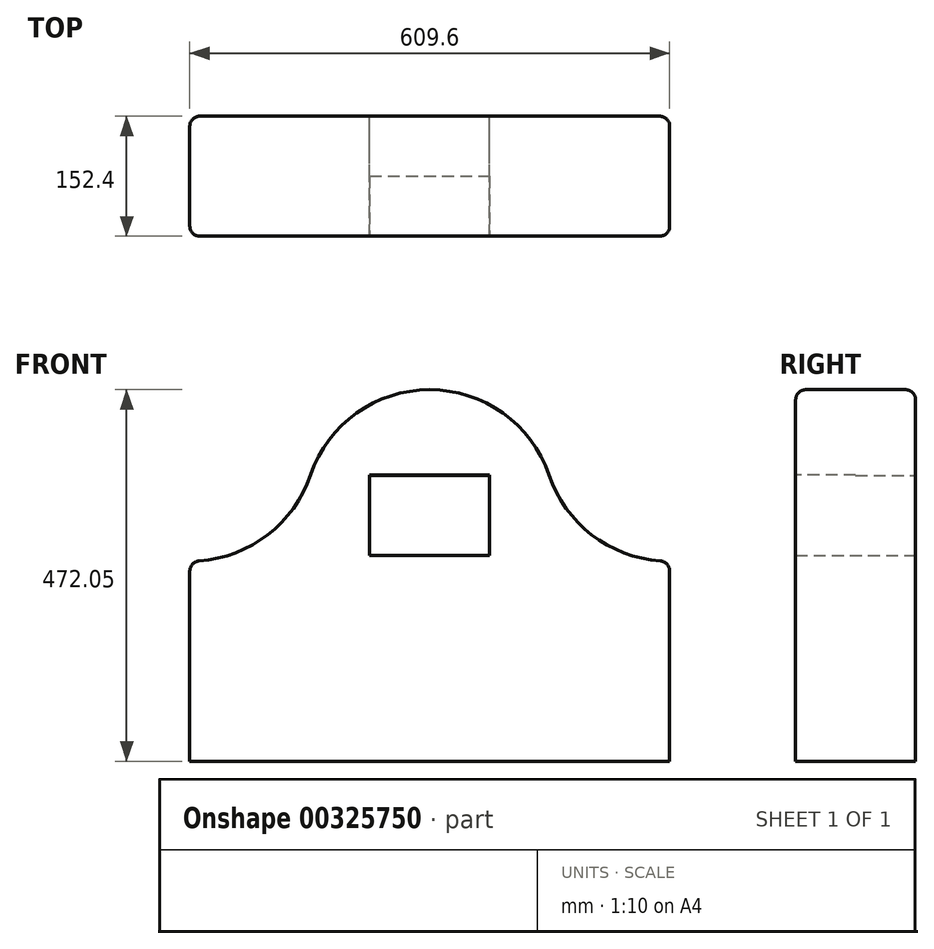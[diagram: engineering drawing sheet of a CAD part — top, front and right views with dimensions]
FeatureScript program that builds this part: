
annotation { "Feature Type Name" : "Feature", "Feature Type Description" : "" }
export const myFeature = defineFeature(function(context is Context, id is Id, definition is map)
    precondition{}
    {
        {
            var Q0;
            Q0=qCreatedBy(makeId("Front.planeOp"),FACE);
            var sketch = newSketch(context, id + "F0", { "sketchPlane" : qUnion([Q0])});
            skLineSegment(sketch, "E0.top", {"start": v(0, -254) * mm, "end": v(609.6, -254) * mm});
            skLineSegment(sketch, "E0.left", {"start": v(0, 0) * mm, "end": v(0, -254) * mm});
            skLineSegment(sketch, "E0.right", {"start": v(609.6, 0) * mm, "end": v(609.6, -254) * mm});
            skArc(sketch, "E1", {"start": v(0, 0) * mm, "mid": v(94.32, 30.26) * mm, "end": v(153.43, 109.76) * mm});
            skArc(sketch, "E2.MirrorCS", {"start": v(609.6, 0) * mm, "mid": v(515.28, 30.26) * mm, "end": v(456.17, 109.76) * mm});
            skArc(sketch, "E3", {"start": v(456.17, 109.76) * mm, "mid": v(304.8, 218.05) * mm, "end": v(153.43, 109.76) * mm});
            skLineSegment(sketch, "E4.bottom", {"start": v(228.6, 108.9) * mm, "end": v(381, 108.9) * mm});
            skLineSegment(sketch, "E4.top", {"start": v(228.6, 7.3) * mm, "end": v(381, 7.3) * mm});
            skLineSegment(sketch, "E4.left", {"start": v(228.6, 108.9) * mm, "end": v(228.6, 7.3) * mm});
            skLineSegment(sketch, "E4.right", {"start": v(381, 108.9) * mm, "end": v(381, 7.3) * mm});
            skSolve(sketch);
        }
        {
            var Q0;
            {var subQ1=sQuery(id+"F0.wireOp",EDGE,"E1");Q0=makeQuery(id+"F0.imprint","IMPRINT",FACE,{"disambiguationData":[TD([[makeQuery(id+"F0.imprint","IMPRINT",EDGE,{"derivedFrom":subQ1}),-1.0]])]});}
            var Q1;
            {var subQ0=sQuery(id+"F0.wireOp",EDGE,"E0.left");Q1=makeQuery(id+"F0.imprint","IMPRINT",FACE,{"disambiguationData":[TD([[makeQuery(id+"F0.imprint","IMPRINT",EDGE,{"derivedFrom":subQ0}),1.0]])]});}
            var Q2;
            {var subQ0=sQuery(id+"F0.wireOp",EDGE,"E0.right");Q2=makeQuery(id+"F0.imprint","IMPRINT",FACE,{"disambiguationData":[TD([[makeQuery(id+"F0.imprint","IMPRINT",EDGE,{"derivedFrom":subQ0}),-1.0]])]});}
            extrude(context, id + "F1", {"entities" : qUnion([Q0, Q1, Q2]), "depth" : 152.4 * mm});
        }
        {
            var Q0;
            Q0=makeQuery(id+"F1.opExtrude","CAP_FACE",FACE,{"disambiguationData":[OSD([sQuery(id+"F0.wireOp",EDGE,"E0.top"),sQuery(id+"F0.wireOp",EDGE,"E0.left"),sQuery(id+"F0.wireOp",EDGE,"E0.right"),sQuery(id+"F0.wireOp",EDGE,"E1"),sQuery(id+"F0.wireOp",EDGE,"E2.MirrorCS"),sQuery(id+"F0.wireOp",EDGE,"E3")])],"isStart":false});
            var sketch = newSketch(context, id + "F2", { "sketchPlane" : qUnion([Q0])});
            skLineSegment(sketch, "E5.0.0", {"start": v(609.6, -254) * mm, "end": v(609.6, 0) * mm});
            skArc(sketch, "E5.0.1", {"start": v(609.6, 0) * mm, "mid": v(515.28, 30.26) * mm, "end": v(456.17, 109.76) * mm});
            skArc(sketch, "E5.0.2", {"start": v(456.17, 109.76) * mm, "mid": v(304.8, 218.05) * mm, "end": v(153.43, 109.76) * mm});
            skArc(sketch, "E5.0.3", {"start": v(153.43, 109.76) * mm, "mid": v(94.32, 30.26) * mm, "end": v(0, 0) * mm});
            skLineSegment(sketch, "E5.0.4", {"start": v(0, 0) * mm, "end": v(0, -254) * mm});
            skLineSegment(sketch, "E5.0.5", {"start": v(0, -254) * mm, "end": v(609.6, -254) * mm});
            skLineSegment(sketch, "E6.bottom", {"start": v(228.6, 109.76) * mm, "end": v(381, 109.76) * mm});
            skLineSegment(sketch, "E6.top", {"start": v(228.6, 0) * mm, "end": v(381, 0) * mm});
            skLineSegment(sketch, "E6.left", {"start": v(228.6, 109.76) * mm, "end": v(228.6, 0) * mm});
            skLineSegment(sketch, "E6.right", {"start": v(381, 109.76) * mm, "end": v(381, 0) * mm});
            skSolve(sketch);
        }
        {
            var Q0;
            Q0=makeQuery(id+"F2.imprint","IMPRINT",FACE,{"disambiguationData":[TD([[makeQuery(id+"F2.imprint","IMPRINT",EDGE,{"derivedFrom":sQuery(id+"F2.wireOp",EDGE,"E6.bottom")}),-1.0]])]});
            extrude(context, id + "F3", {"entities" : qUnion([Q0]), "operationType" : NewBodyOperationType.REMOVE, "oppositeDirection" : true, "depth" : 76.2 * mm});
        }
        {
            var Q0;
            Q0=makeQuery(id+"F1.opExtrude","SWEPT_EDGE",EDGE,{"disambiguationData":[OSD([sQuery(id+"F0.wireOp",EDGE,"E0.bottom"),sQuery(id+"F0.wireOp",EDGE,"E0.right"),sQuery(id+"F0.wireOp",EDGE,"E2.MirrorCS")])]});
            var Q1;
            Q1=makeQuery(id+"F1.opExtrude","SWEPT_EDGE",EDGE,{"disambiguationData":[OSD([sQuery(id+"F0.wireOp",EDGE,"E0.bottom"),sQuery(id+"F0.wireOp",EDGE,"E0.left"),sQuery(id+"F0.wireOp",EDGE,"E1")])]});
            var Q2;
            Q2=makeQuery(id+"F1.opExtrude","CAP_EDGE",EDGE,{"disambiguationData":[OSD([sQuery(id+"F0.wireOp",EDGE,"E2.MirrorCS")])],"isStart":false});
            var Q3;
            Q3=makeQuery(id+"F1.opExtrude","CAP_EDGE",EDGE,{"disambiguationData":[OSD([sQuery(id+"F0.wireOp",EDGE,"E3")])],"isStart":false});
            var Q4;
            Q4=makeQuery(id+"F1.opExtrude","CAP_EDGE",EDGE,{"disambiguationData":[OSD([sQuery(id+"F0.wireOp",EDGE,"E3")])],"isStart":true});
            var Q5;
            Q5=makeQuery(id+"F1.opExtrude","CAP_EDGE",EDGE,{"disambiguationData":[OSD([sQuery(id+"F0.wireOp",EDGE,"E2.MirrorCS")])],"isStart":true});
            var Q6;
            Q6=makeQuery(id+"F1.opExtrude","CAP_EDGE",EDGE,{"disambiguationData":[OSD([sQuery(id+"F0.wireOp",EDGE,"E0.right")])],"isStart":false});
            var Q7;
            Q7=makeQuery(id+"F1.opExtrude","CAP_EDGE",EDGE,{"disambiguationData":[OSD([sQuery(id+"F0.wireOp",EDGE,"E0.right")])],"isStart":true});
            var Q8;
            Q8=makeQuery(id+"F1.opExtrude","CAP_EDGE",EDGE,{"disambiguationData":[OSD([sQuery(id+"F0.wireOp",EDGE,"E0.left")])],"isStart":false});
            var Q9;
            Q9=makeQuery(id+"F1.opExtrude","CAP_EDGE",EDGE,{"disambiguationData":[OSD([sQuery(id+"F0.wireOp",EDGE,"E0.left")])],"isStart":true});
            fillet(context, id + "F4", {"entities" : qUnion([Q0, Q1, Q2, Q3, Q4, Q5, Q6, Q7, Q8, Q9]), "radius" : 12.7 * mm, "tangentPropagation" : true, "allowEdgeOverflow" : false});
        }
    });
